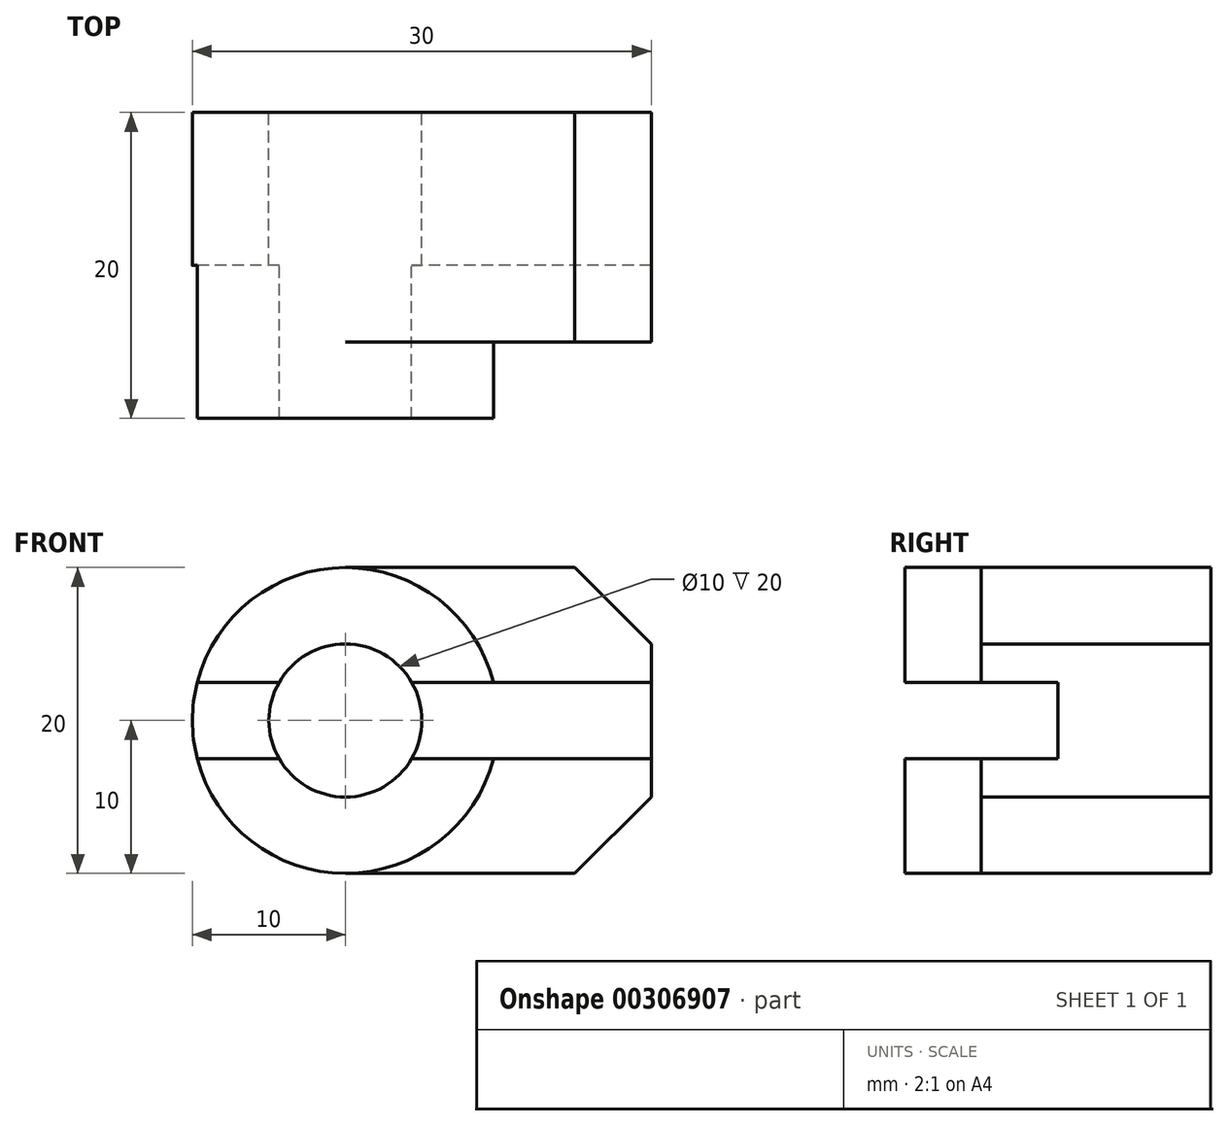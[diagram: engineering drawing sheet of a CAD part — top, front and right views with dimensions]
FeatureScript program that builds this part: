
annotation { "Feature Type Name" : "Feature", "Feature Type Description" : "" }
export const myFeature = defineFeature(function(context is Context, id is Id, definition is map)
    precondition{}
    {
        {
            var Q0;
            Q0=qCreatedBy(makeId("Front.planeOp"),FACE);
            var sketch = newSketch(context, id + "F0", { "sketchPlane" : qUnion([Q0])});
            skCircle(sketch, "E0", {"center": v(0, 0) * mm, "radius": 10 * mm});
            skCircle(sketch, "E1", {"center": v(0, 0) * mm, "radius": 5 * mm});
            skSolve(sketch);
        }
        {
            var Q0;
            Q0 = qSketchRegion(id + "F0", true);
            extrude(context, id + "F1", {"entities" : qUnion([Q0]), "endBound" : BoundingType.SYMMETRIC, "depth" : 20 * mm});
        }
        {
            var Q0;
            Q0=qCreatedBy(makeId("Front.planeOp"),FACE);
            var sketch = newSketch(context, id + "F2", { "sketchPlane" : qUnion([Q0])});
            skLineSegment(sketch, "E2", {"start": v(0, 10) * mm, "end": v(15, 10) * mm});
            skLineSegment(sketch, "E3", {"start": v(15, -10) * mm, "end": v(0, -10) * mm});
            skLineSegment(sketch, "E4", {"start": v(15, 10) * mm, "end": v(20, 5) * mm});
            skLineSegment(sketch, "E5", {"start": v(15, -10) * mm, "end": v(20, -5) * mm});
            skLineSegment(sketch, "E6", {"start": v(20, 5) * mm, "end": v(20, -5) * mm});
            skLineSegment(sketch, "E7", {"start": v(10, 0) * mm, "end": v(20, 0) * mm, "construction": true});
            skArc(sketch, "E8", {"start": v(0, -10) * mm, "mid": v(10, 0) * mm, "end": v(0, 10) * mm});
            skSolve(sketch);
        }
        {
            var Q0;
            Q0 = qSketchRegion(id + "F2", true);
            extrude(context, id + "F3", {"entities" : qUnion([Q0]), "operationType" : NewBodyOperationType.ADD, "endBound" : BoundingType.SYMMETRIC, "depth" : 20 * mm});
        }
        {
            var Q0;
            Q0=makeQuery(id+"F3.boolean.opBoolean","MERGE",FACE,{"derivedFrom":[makeQuery(id+"F1.opExtrude","CAP_FACE",FACE,{"disambiguationData":[OSD([sQuery(id+"F0.wireOp",EDGE,"E0"),sQuery(id+"F0.wireOp",EDGE,"E1")])],"isStart":false}),makeQuery(id+"F3.opExtrude","CAP_FACE",FACE,{"disambiguationData":[OSD([sQuery(id+"F2.wireOp",EDGE,"E2"),sQuery(id+"F2.wireOp",EDGE,"E3"),sQuery(id+"F2.wireOp",EDGE,"E4"),sQuery(id+"F2.wireOp",EDGE,"E5"),sQuery(id+"F2.wireOp",EDGE,"E6"),sQuery(id+"F2.wireOp",EDGE,"E8")])],"isStart":false})]});
            var sketch = newSketch(context, id + "F4", { "sketchPlane" : qUnion([Q0])});
            skArc(sketch, "E9", {"start": v(0, -10) * mm, "mid": v(10, 0) * mm, "end": v(0, 10) * mm});
            skLineSegment(sketch, "E10", {"start": v(0, 10) * mm, "end": v(15, 10) * mm});
            skLineSegment(sketch, "E11", {"start": v(15, 10) * mm, "end": v(20, 5) * mm});
            skLineSegment(sketch, "E12", {"start": v(20, 5) * mm, "end": v(20, -5) * mm});
            skLineSegment(sketch, "E13", {"start": v(20, -5) * mm, "end": v(15, -10) * mm});
            skLineSegment(sketch, "E14", {"start": v(15, -10) * mm, "end": v(0, -10) * mm});
            skSolve(sketch);
        }
        {
            var Q0;
            Q0 = qSketchRegion(id + "F4", true);
            extrude(context, id + "F5", {"entities" : qUnion([Q0]), "operationType" : NewBodyOperationType.REMOVE, "oppositeDirection" : true, "depth" : 5 * mm});
        }
        {
            var Q0;
            Q0=qCreatedBy(makeId("Front.planeOp"),FACE);
            var sketch = newSketch(context, id + "F6", { "sketchPlane" : qUnion([Q0])});
            skLineSegment(sketch, "E15", {"start": v(-9.68, 2.5) * mm, "end": v(20.32, 2.5) * mm});
            skLineSegment(sketch, "E16", {"start": v(20.32, 2.5) * mm, "end": v(20.32, -2.5) * mm});
            skLineSegment(sketch, "E17", {"start": v(20.32, -2.5) * mm, "end": v(-9.68, -2.5) * mm});
            skArc(sketch, "E18", {"start": v(-9.68, 2.5) * mm, "mid": v(-10, 0) * mm, "end": v(-9.68, -2.5) * mm});
            skSolve(sketch);
        }
        {
            var Q0;
            Q0 = qSketchRegion(id + "F6", true);
            extrude(context, id + "F7", {"entities" : qUnion([Q0]), "operationType" : NewBodyOperationType.REMOVE, "depth" : 10 * mm});
        }
    });
